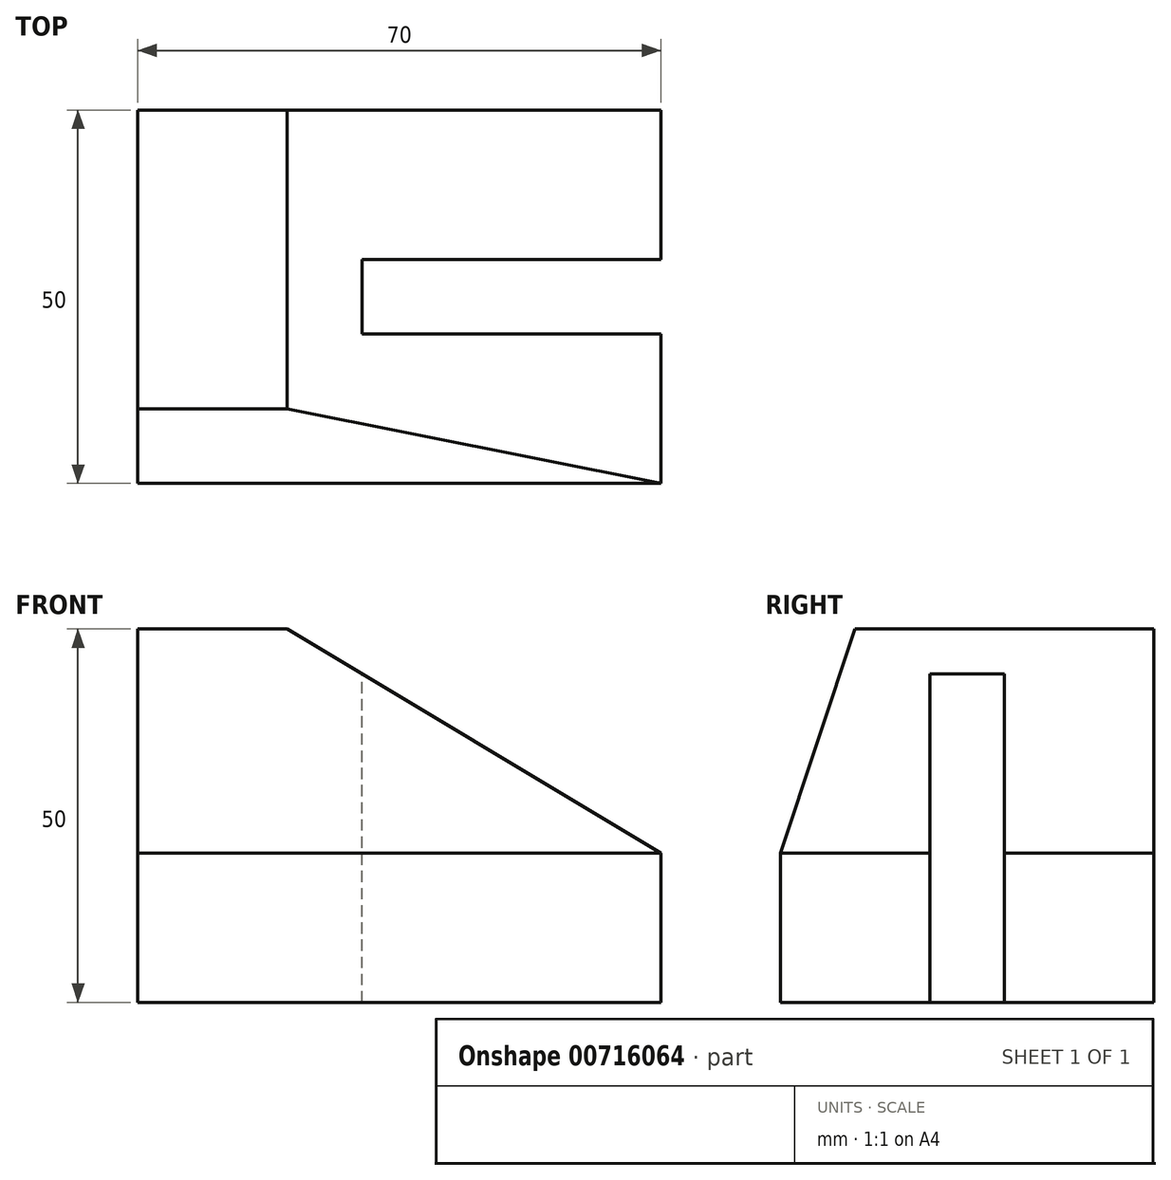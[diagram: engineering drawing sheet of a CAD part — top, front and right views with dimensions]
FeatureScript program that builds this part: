
annotation { "Feature Type Name" : "Feature", "Feature Type Description" : "" }
export const myFeature = defineFeature(function(context is Context, id is Id, definition is map)
    precondition{}
    {
        {
            var Q0;
            Q0=qCreatedBy(makeId("Top.planeOp"),FACE);
            var sketch = newSketch(context, id + "F0", { "sketchPlane" : qUnion([Q0])});
            skLineSegment(sketch, "E0.bottom", {"start": v(0, -25) * mm, "end": v(70, -25) * mm});
            skLineSegment(sketch, "E0.top", {"start": v(0, 25) * mm, "end": v(70, 25) * mm});
            skLineSegment(sketch, "E0.left", {"start": v(0, -25) * mm, "end": v(0, 25) * mm});
            skLineSegment(sketch, "E0.right", {"start": v(70, -25) * mm, "end": v(70, 25) * mm});
            skSolve(sketch);
        }
        {
            var Q0;
            Q0=makeQuery(id+"F0.imprint","IMPRINT",FACE,{"disambiguationData":[TD([[makeQuery(id+"F0.imprint","IMPRINT",EDGE,{"derivedFrom":sQuery(id+"F0.wireOp",EDGE,"E0.bottom")}),1.0]])]});
            extrude(context, id + "F1", {"entities" : qUnion([Q0]), "depth" : 20 * mm, "offsetDistance" : 25 * mm});
        }
        {
            var Q0;
            Q0=makeQuery(id+"F1.opExtrude","SWEPT_FACE",FACE,{"disambiguationData":[OSD([sQuery(id+"F0.wireOp",EDGE,"E0.bottom")])]});
            var sketch = newSketch(context, id + "F2", { "sketchPlane" : qUnion([Q0])});
            skLineSegment(sketch, "E1", {"start": v(0, 20) * mm, "end": v(0, 50) * mm});
            skLineSegment(sketch, "E2", {"start": v(0, 50) * mm, "end": v(20, 50) * mm});
            skLineSegment(sketch, "E3", {"start": v(20, 50) * mm, "end": v(70, 20) * mm});
            skLineSegment(sketch, "E4", {"start": v(70, 20) * mm, "end": v(0, 20) * mm});
            skSolve(sketch);
        }
        {
            var Q0;
            Q0=makeQuery(id+"F2.imprint","IMPRINT",FACE,{"disambiguationData":[TD([[makeQuery(id+"F2.imprint","IMPRINT",EDGE,{"derivedFrom":sQuery(id+"F2.wireOp",EDGE,"E1")}),-1.0]])]});
            var Q1;
            Q1=makeQuery(id+"F1.opExtrude","SWEPT_FACE",FACE,{"disambiguationData":[OSD([sQuery(id+"F0.wireOp",EDGE,"E0.top")])]});
            extrude(context, id + "F3", {"entities" : qUnion([Q0]), "operationType" : NewBodyOperationType.ADD, "endBound" : BoundingType.UP_TO_SURFACE, "oppositeDirection" : true, "depth" : 25 * mm, "endBoundEntityFace" : qUnion([Q1]), "offsetDistance" : 25 * mm});
        }
        {
            var Q0;
            Q0=makeQuery(id+"F3.boolean.opBoolean","MERGE",FACE,{"derivedFrom":[makeQuery(id+"F1.opExtrude","SWEPT_FACE",FACE,{"disambiguationData":[OSD([sQuery(id+"F0.wireOp",EDGE,"E0.left")])]}),makeQuery(id+"F3.opExtrude","SWEPT_FACE",FACE,{"disambiguationData":[OSD([sQuery(id+"F2.wireOp",EDGE,"E1")])]})]});
            var sketch = newSketch(context, id + "F4", { "sketchPlane" : qUnion([Q0])});
            skLineSegment(sketch, "E5", {"start": v(25, 50) * mm, "end": v(15, 50) * mm});
            skLineSegment(sketch, "E6", {"start": v(15, 50) * mm, "end": v(25, 20) * mm});
            skLineSegment(sketch, "E7", {"start": v(25, 20) * mm, "end": v(25, 50) * mm});
            skSolve(sketch);
        }
        {
            var Q0;
            Q0 = qSketchRegion(id + "F4", true);
            extrude(context, id + "F5", {"entities" : qUnion([Q0]), "operationType" : NewBodyOperationType.REMOVE, "endBound" : BoundingType.UP_TO_NEXT, "oppositeDirection" : true, "depth" : 25 * mm, "offsetDistance" : 25 * mm});
        }
        {
            var Q0;
            Q0=makeQuery(id+"F3.opExtrude","SWEPT_FACE",FACE,{"disambiguationData":[OSD([sQuery(id+"F2.wireOp",EDGE,"E2")])]});
            var sketch = newSketch(context, id + "F6", { "sketchPlane" : qUnion([Q0])});
            skLineSegment(sketch, "E8.bottom", {"start": v(30, -5) * mm, "end": v(70, -5) * mm});
            skLineSegment(sketch, "E8.top", {"start": v(30, 5) * mm, "end": v(70, 5) * mm});
            skLineSegment(sketch, "E8.left", {"start": v(30, -5) * mm, "end": v(30, 5) * mm});
            skLineSegment(sketch, "E8.right", {"start": v(70, -5) * mm, "end": v(70, 5) * mm});
            skSolve(sketch);
        }
        {
            var Q0;
            Q0 = qSketchRegion(id + "F6", true);
            extrude(context, id + "F7", {"entities" : qUnion([Q0]), "operationType" : NewBodyOperationType.REMOVE, "endBound" : BoundingType.THROUGH_ALL, "oppositeDirection" : true, "depth" : 25 * mm, "offsetDistance" : 25 * mm});
        }
    });
